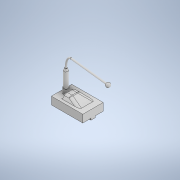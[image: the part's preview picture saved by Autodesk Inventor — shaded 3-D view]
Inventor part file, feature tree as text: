
AUTODESK INVENTOR PART (.ipt)
format: ipt  version: 2021 (Build 250183000, 183)  size: 252,928 bytes
history: native  units: mm
features: sketch x12, extrude x7, other x4, chamfer x2, plane x1, loft x1, sweep x1, fillet x1, projected_geometry x1
ambient origin geometry x8: Origin, YZ Plane, XZ Plane, XY Plane, X Axis, Y Axis, Z Axis, Center Point
bodies: Body1 (feature_tree), Body2 (feature_tree)
feature tree (30):
  other  "實體1"
  extrude  "擠出1"  Depth=152.4mm
  extrude  "擠出2"  Depth=99.2mm
  extrude  "擠出3"  Depth=37.0mm TaperAngle=0.0deg
  extrude  "擠出4"  Depth=20.0mm
  extrude  "擠出5"  Depth=11.0mm
  plane  "工作平面1"
  loft  "斷面混成1"
  sweep  "掃掠1"
  other  "迴轉1"
  chamfer  "倒角1"  Distance=72.0mm
  chamfer  "倒角2"  Distance=16.0mm
  fillet  "圓角1"  Radius=25.0mm
  extrude  "擠出6"  Depth=21.0mm
  extrude  "擠出7"  Depth=34.0mm
  sketch  "草圖1"
  sketch  "草圖2"
  sketch  "草圖3"
  sketch  "草圖4"
  sketch  "草圖5"
  sketch  "草圖6"
  sketch  "草圖7"
  other  "Srf1"
  sketch  "草圖8"
  sketch  "草圖9"
  sketch  "草圖10"
  sketch  "草圖11"
  sketch  "草圖12"
  projected_geometry  "投影迴路1"
  other  "擠出表面1"
